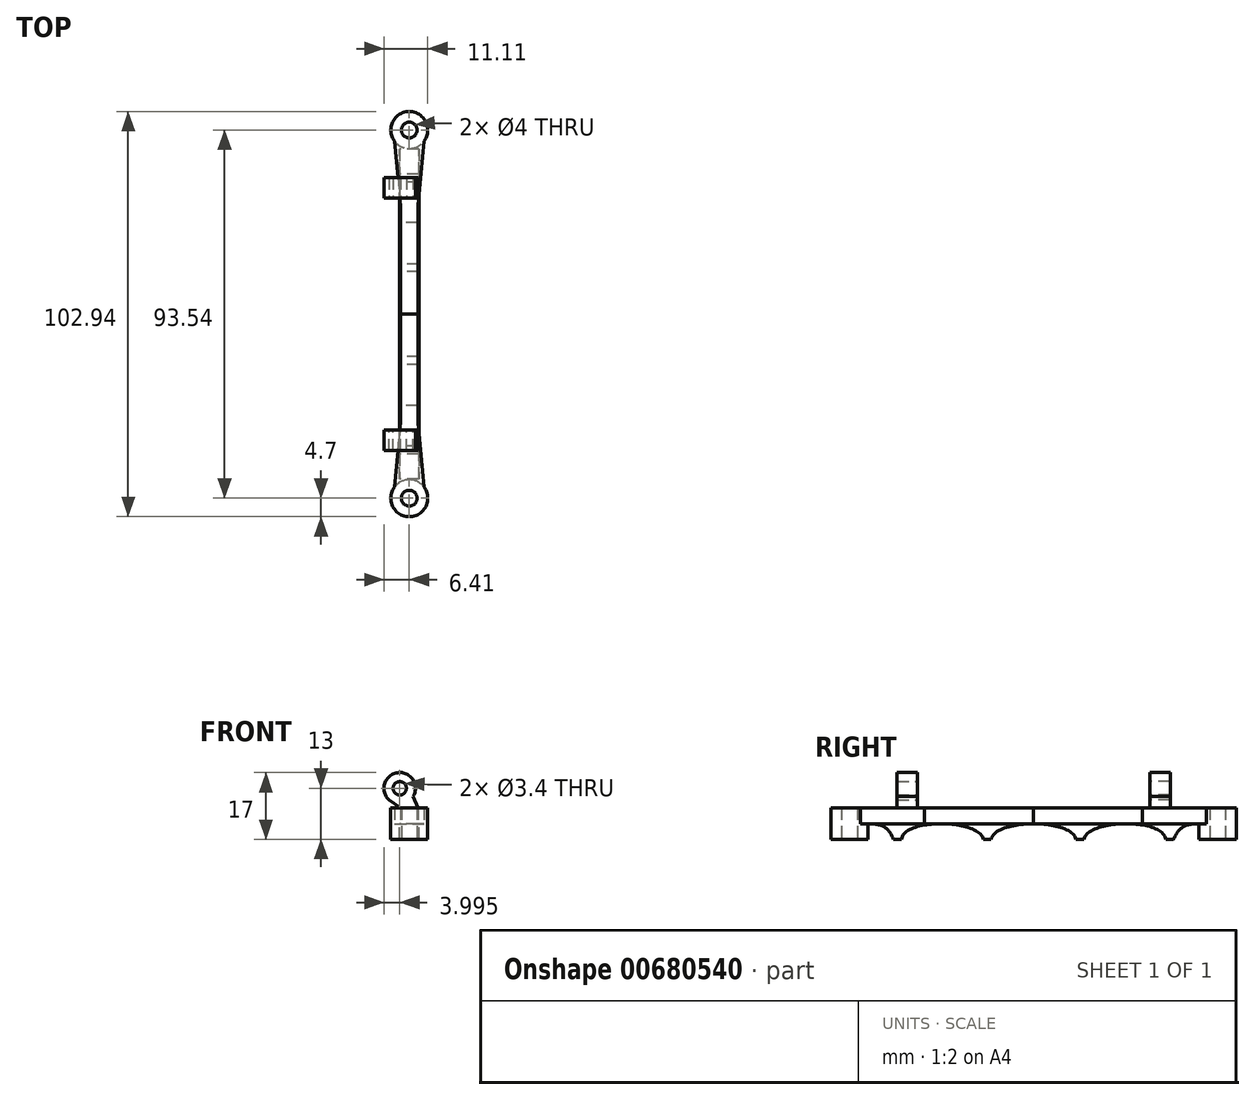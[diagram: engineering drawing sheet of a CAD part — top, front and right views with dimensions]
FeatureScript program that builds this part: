
annotation { "Feature Type Name" : "Feature", "Feature Type Description" : "" }
export const myFeature = defineFeature(function(context is Context, id is Id, definition is map)
    precondition{}
    {
        {
            var Q0;
            Q0=qCreatedBy(makeId("Top.planeOp"),FACE);
            var sketch = newSketch(context, id + "F0", { "sketchPlane" : qUnion([Q0])});
            skCircle(sketch, "E0", {"center": v(0, 46.77) * mm, "radius": 2 * mm});
            skCircle(sketch, "E1", {"center": v(0, 46.77) * mm, "radius": 4.7 * mm});
            skLineSegment(sketch, "E2", {"start": v(-2.25, 0) * mm, "end": v(0, 0) * mm});
            skLineSegment(sketch, "E3", {"start": v(-3.74, 43.92) * mm, "end": v(-2.25, 27.7) * mm});
            skLineSegment(sketch, "E4", {"start": v(-2.25, 27.7) * mm, "end": v(-2.25, 0) * mm});
            skLineSegment(sketch, "E5.MirrorCS", {"start": v(3.74, 43.92) * mm, "end": v(2.25, 27.7) * mm});
            skLineSegment(sketch, "E6.MirrorCS", {"start": v(2.25, 27.7) * mm, "end": v(2.25, 0) * mm});
            skLineSegment(sketch, "E7.MirrorCS", {"start": v(2.25, 0) * mm, "end": v(0, 0) * mm});
            skSolve(sketch);
        }
        {
            var Q0;
            Q0=makeQuery(id+"F0.imprint","IMPRINT",FACE,{"disambiguationData":[TD([[makeQuery(id+"F0.imprint","IMPRINT",EDGE,{"derivedFrom":sQuery(id+"F0.wireOp",EDGE,"E2")}),1.0]])]});
            var Q1;
            {var subQ1=sQuery(id+"F0.wireOp",EDGE,"E3");Q1=makeQuery(id+"F0.imprint","IMPRINT",FACE,{"disambiguationData":[TD([[makeQuery(id+"F0.imprint","IMPRINT",EDGE,{"derivedFrom":subQ1}),1.0]])]});}
            var Q2;
            Q2=makeQuery(id+"F0.imprint","IMPRINT",FACE,{"disambiguationData":[TD([[makeQuery(id+"F0.imprint","IMPRINT",EDGE,{"derivedFrom":sQuery(id+"F0.wireOp",EDGE,"E0")}),-1.0]])]});
            extrude(context, id + "F1", {"entities" : qUnion([Q0, Q1, Q2]), "depth" : 4 * mm, "offsetDistance" : 25 * mm});
        }
        {
            var Q0;
            Q0=qCreatedBy(makeId("Front.planeOp"),FACE);
            var sketch = newSketch(context, id + "F2", { "sketchPlane" : qUnion([Q0])});
            skCircle(sketch, "E8", {"center": v(-2.41, 9) * mm, "radius": 4 * mm});
            skCircle(sketch, "E9", {"center": v(-2.41, 9) * mm, "radius": 1.7 * mm});
            skLineSegment(sketch, "E10", {"start": v(1, 6.93) * mm, "end": v(2.25, 4) * mm});
            skLineSegment(sketch, "E11", {"start": v(-5.1, 6.04) * mm, "end": v(-2.25, 4) * mm});
            skLineSegment(sketch, "E12", {"start": v(-2.25, 4) * mm, "end": v(2.25, 4) * mm});
            skSolve(sketch);
        }
        {
            var Q0;
            {var subQ0=sQuery(id+"F2.wireOp",EDGE,"E10");Q0=makeQuery(id+"F2.imprint","IMPRINT",FACE,{"disambiguationData":[TD([[makeQuery(id+"F2.imprint","IMPRINT",EDGE,{"derivedFrom":subQ0}),-1.0]])]});}
            var Q1;
            Q1=makeQuery(id+"F2.imprint","IMPRINT",FACE,{"disambiguationData":[TD([[makeQuery(id+"F2.imprint","IMPRINT",EDGE,{"derivedFrom":sQuery(id+"F2.wireOp",EDGE,"E9")}),-1.0]])]});
            extrude(context, id + "F3", {"entities" : qUnion([Q0, Q1]), "operationType" : NewBodyOperationType.ADD, "oppositeDirection" : true, "depth" : 34.7 * mm, "offsetDistance" : 25 * mm, "hasSecondDirection" : true, "secondDirectionOppositeDirection" : false, "secondDirectionDepth" : -29.5 * mm});
        }
        {
            var Q0;
            Q0=makeQuery(id+"F0.imprint","IMPRINT",FACE,{"disambiguationData":[TD([[makeQuery(id+"F0.imprint","IMPRINT",EDGE,{"derivedFrom":sQuery(id+"F0.wireOp",EDGE,"E0")}),-1.0]])]});
            extrude(context, id + "F4", {"entities" : qUnion([Q0]), "operationType" : NewBodyOperationType.ADD, "depth" : -4 * mm, "offsetDistance" : 25 * mm});
        }
        {
            var Q0;
            Q0=qCreatedBy(makeId("Right.planeOp"),FACE);
            var sketch = newSketch(context, id + "F5", { "sketchPlane" : qUnion([Q0])});
            skLineSegment(sketch, "E13", {"start": v(35.57, 0) * mm, "end": v(35.57, -4) * mm});
            skLineSegment(sketch, "E14", {"start": v(35.57, -4) * mm, "end": v(33.57, -4) * mm});
            skLineSegment(sketch, "E15", {"start": v(23.26, 0) * mm, "end": v(35.57, 0) * mm});
            skLineSegment(sketch, "E16", {"start": v(41.9, 0) * mm, "end": v(35.57, 0) * mm});
            skLineSegment(sketch, "E17", {"start": v(12.77, -4) * mm, "end": v(10.77, -4) * mm});
            skLineSegment(sketch, "E18", {"start": v(0, 0) * mm, "end": v(23.26, 0) * mm});
            skFitSpline(sketch, "E19", {"points": [v(12.77, -4) * mm, v(23.26, 0) * mm], "startDerivative": vector(1.64, 9.06) * mm, "endDerivative": vector(10.62, 0) * mm});
            skFitSpline(sketch, "E20", {"points": [v(23.26, 0) * mm, v(33.57, -4) * mm], "startDerivative": vector(12.06, 0) * mm, "endDerivative": vector(1.28, -9.5) * mm});
            skFitSpline(sketch, "E21", {"points": [v(35.57, -4) * mm, v(41.9, 0) * mm], "startDerivative": vector(3.77, 9.64) * mm, "endDerivative": vector(9.5, 0) * mm});
            skFitSpline(sketch, "E22", {"points": [v(10.77, -4) * mm, v(0, 0) * mm], "startDerivative": vector(-1.8, 9.2) * mm, "endDerivative": vector(-11.3, 0) * mm});
            skSolve(sketch);
        }
        {
            var Q0;
            Q0=makeQuery(id+"F5.imprint","IMPRINT",FACE,{"disambiguationData":[TD([[makeQuery(id+"F5.imprint","IMPRINT",EDGE,{"derivedFrom":sQuery(id+"F5.wireOp",EDGE,"E13")}),1.0]])]});
            var Q1;
            Q1=makeQuery(id+"F5.imprint","IMPRINT",FACE,{"disambiguationData":[TD([[makeQuery(id+"F5.imprint","IMPRINT",EDGE,{"derivedFrom":sQuery(id+"F5.wireOp",EDGE,"E13")}),-1.0]])]});
            var Q2;
            Q2=makeQuery(id+"F5.imprint","IMPRINT",FACE,{"disambiguationData":[TD([[makeQuery(id+"F5.imprint","IMPRINT",EDGE,{"derivedFrom":sQuery(id+"F5.wireOp",EDGE,"OMmC7Q2a-5Xuo-Fr55-cwD3-ILsq5TRR48wA")}),-1.0]])]});
            var Q3;
            Q3=makeQuery(id+"F5.imprint","IMPRINT",FACE,{"disambiguationData":[TD([[makeQuery(id+"F5.imprint","IMPRINT",EDGE,{"derivedFrom":sQuery(id+"F5.wireOp",EDGE,"E17")}),-1.0]])]});
            extrude(context, id + "F6", {"entities" : qUnion([Q0, Q1, Q2, Q3]), "endBound" : BoundingType.SYMMETRIC, "depth" : 5 * mm, "offsetDistance" : 25 * mm});
        }
        {
            var Q0;
            Q0=makeQuery(id+"F1.opExtrude","SWEPT_BODY",BODY,{"disambiguationData":[OSD([sQuery(id+"F0.wireOp",EDGE,"E0"),sQuery(id+"F0.wireOp",EDGE,"E1"),sQuery(id+"F0.wireOp",EDGE,"E2"),sQuery(id+"F0.wireOp",EDGE,"E3"),sQuery(id+"F0.wireOp",EDGE,"E4"),sQuery(id+"F0.wireOp",EDGE,"E5.MirrorCS"),sQuery(id+"F0.wireOp",EDGE,"E6.MirrorCS"),sQuery(id+"F0.wireOp",EDGE,"E7.MirrorCS")])]});
            var Q1;
            Q1=makeQuery(id+"F6.opExtrude","SWEPT_BODY",BODY,{"disambiguationData":[OSD([sQuery(id+"F5.wireOp",EDGE,"E14"),sQuery(id+"F5.wireOp",EDGE,"E15"),sQuery(id+"F5.wireOp",EDGE,"E16"),sQuery(id+"F5.wireOp",EDGE,"E20"),sQuery(id+"F5.wireOp",EDGE,"E21")])]});
            var Q2;
            Q2=makeQuery(id+"F6.opExtrude","SWEPT_BODY",BODY,{"disambiguationData":[OSD([sQuery(id+"F5.wireOp",EDGE,"E17"),sQuery(id+"F5.wireOp",EDGE,"E18"),sQuery(id+"F5.wireOp",EDGE,"E19"),sQuery(id+"F5.wireOp",EDGE,"E22")])]});
            var Q3;
            Q3=makeQuery(id+"F1.opExtrude","SWEPT_FACE",FACE,{"disambiguationData":[OSD([sQuery(id+"F0.wireOp",EDGE,"E2"),sQuery(id+"F0.wireOp",EDGE,"E7.MirrorCS")])]});
            mirror(context, id + "F7", {"entities" : qUnion([Q0, Q1, Q2]), "mirrorPlane" : qUnion([Q3])});
        }
    });
